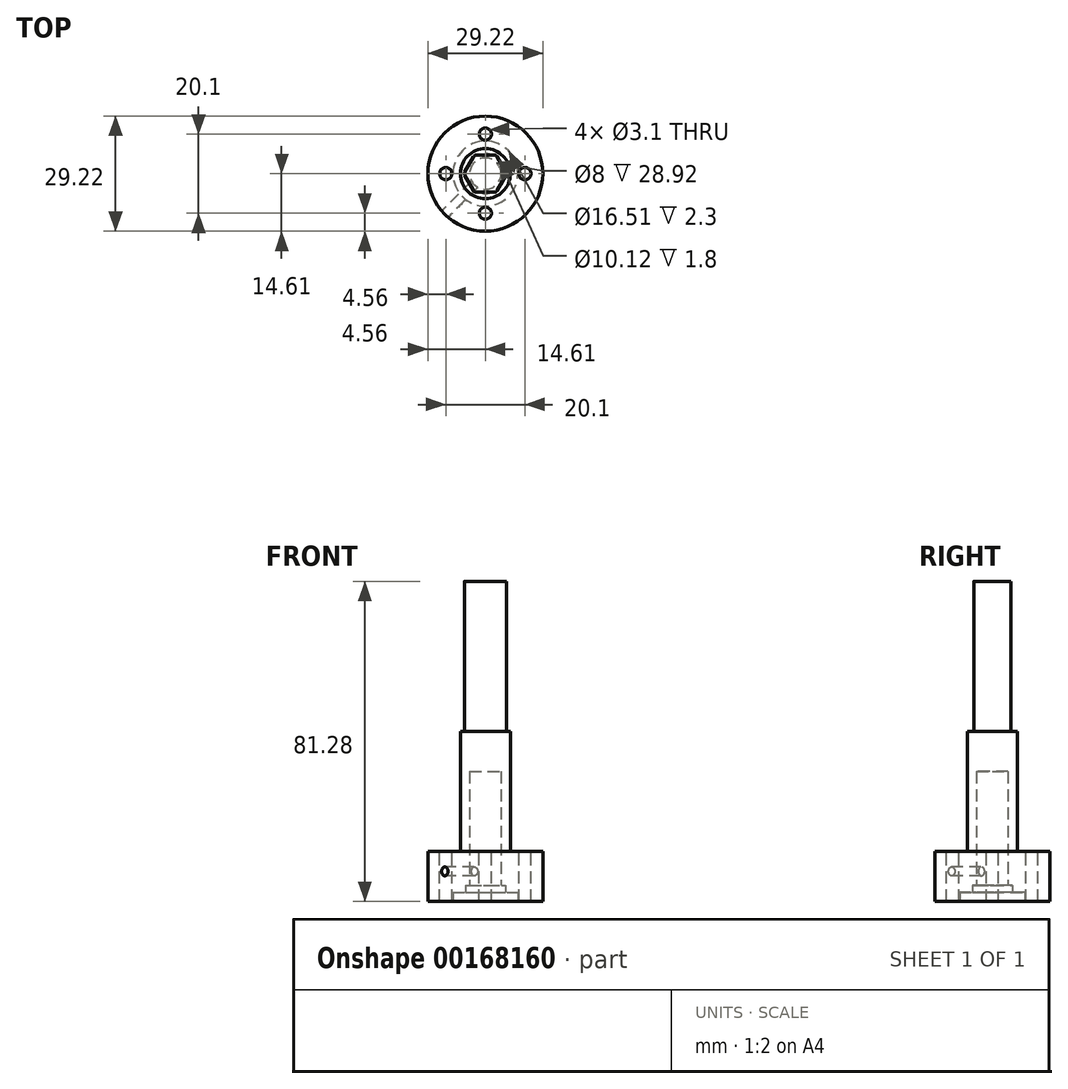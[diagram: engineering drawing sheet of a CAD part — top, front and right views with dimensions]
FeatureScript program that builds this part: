
annotation { "Feature Type Name" : "Feature", "Feature Type Description" : "" }
export const myFeature = defineFeature(function(context is Context, id is Id, definition is map)
    precondition{}
    {
        {
            var Q0;
            Q0=qCreatedBy(makeId("Top.planeOp"),FACE);
            var sketch = newSketch(context, id + "F0", { "sketchPlane" : qUnion([Q0])});
            skCircle(sketch, "E0", {"center": v(0, 0) * mm, "radius": 14.6 * mm});
            skSolve(sketch);
        }
        {
            var Q0;
            Q0=makeQuery(id+"F0.imprint","IMPRINT",FACE,{"disambiguationData":[TD([[makeQuery(id+"F0.imprint","IMPRINT",EDGE,{"derivedFrom":sQuery(id+"F0.wireOp",EDGE,"E0")}),1.0]])]});
            extrude(context, id + "F1", {"entities" : qUnion([Q0]), "depth" : 12.7 * mm});
        }
        {
            var Q0;
            Q0=makeQuery(id+"F1.opExtrude","CAP_FACE",FACE,{"disambiguationData":[OSD([sQuery(id+"F0.wireOp",EDGE,"E0")])],"isStart":false});
            var sketch = newSketch(context, id + "F2", { "sketchPlane" : qUnion([Q0])});
            skCircle(sketch, "E1", {"center": v(0, 0) * mm, "radius": 6.35 * mm});
            skSolve(sketch);
        }
        {
            var Q0;
            Q0=qSketchRegion(id+"F2",true);
            extrude(context, id + "F3", {"entities" : qUnion([Q0]), "operationType" : NewBodyOperationType.ADD, "depth" : 30.48 * mm});
        }
        {
            var Q0;
            Q0=makeQuery(id+"F3.opExtrude","CAP_FACE",FACE,{"disambiguationData":[OSD([sQuery(id+"F2.wireOp",EDGE,"E1")])],"isStart":false});
            var sketch = newSketch(context, id + "F4", { "sketchPlane" : qUnion([Q0])});
            skCircle(sketch, "E2.cCircle", {"center": v(0, 0) * mm, "radius": 4.72 * mm, "construction": true});
            skLineSegment(sketch, "E2.0", {"start": v(5.46, 0) * mm, "end": v(2.73, -4.72) * mm});
            skLineSegment(sketch, "E2.1", {"start": v(2.73, -4.72) * mm, "end": v(-2.73, -4.72) * mm});
            skLineSegment(sketch, "E2.2", {"start": v(-2.73, -4.72) * mm, "end": v(-5.46, 0) * mm});
            skLineSegment(sketch, "E2.3", {"start": v(-5.46, 0) * mm, "end": v(-2.73, 4.72) * mm});
            skLineSegment(sketch, "E2.4", {"start": v(-2.73, 4.72) * mm, "end": v(2.73, 4.72) * mm});
            skLineSegment(sketch, "E2.5", {"start": v(2.73, 4.72) * mm, "end": v(5.46, 0) * mm});
            skPoint(sketch, "E2.0.midPoint", {"position": v(4.1, -2.36) * mm});
            skSolve(sketch);
        }
        {
            var Q0;
            Q0=makeQuery(id+"F4.imprint","IMPRINT",FACE,{"disambiguationData":[TD([[makeQuery(id+"F4.imprint","IMPRINT",EDGE,{"derivedFrom":sQuery(id+"F4.wireOp",EDGE,"E2.0")}),-1.0]])]});
            extrude(context, id + "F5", {"entities" : qUnion([Q0]), "operationType" : NewBodyOperationType.ADD, "depth" : 38.1 * mm});
        }
        {
            var Q0;
            Q0=makeQuery(id+"F1.opExtrude","CAP_FACE",FACE,{"disambiguationData":[OSD([sQuery(id+"F0.wireOp",EDGE,"E0")])],"isStart":true});
            var sketch = newSketch(context, id + "F6", { "sketchPlane" : qUnion([Q0])});
            skCircle(sketch, "E3", {"center": v(0, 0) * mm, "radius": 8.26 * mm});
            skSolve(sketch);
        }
        {
            var Q0;
            Q0=qSketchRegion(id+"F6",true);
            extrude(context, id + "F7", {"entities" : qUnion([Q0]), "operationType" : NewBodyOperationType.REMOVE, "oppositeDirection" : true, "depth" : 2.3 * mm});
        }
        {
            var Q0;
            Q0=makeQuery(id+"F1.opExtrude","CAP_FACE",FACE,{"disambiguationData":[OSD([sQuery(id+"F0.wireOp",EDGE,"E0")])],"isStart":true});
            var sketch = newSketch(context, id + "F8", { "sketchPlane" : qUnion([Q0])});
            skCircle(sketch, "E4", {"center": v(0, 0) * mm, "radius": 5.06 * mm});
            skSolve(sketch);
        }
        {
            var Q0;
            Q0=qSketchRegion(id+"F8",true);
            extrude(context, id + "F9", {"entities" : qUnion([Q0]), "operationType" : NewBodyOperationType.REMOVE, "oppositeDirection" : true, "depth" : 4.1 * mm});
        }
        {
            var Q0;
            Q0=makeQuery(id+"F1.opExtrude","CAP_FACE",FACE,{"disambiguationData":[OSD([sQuery(id+"F0.wireOp",EDGE,"E0")])],"isStart":false});
            var sketch = newSketch(context, id + "F10", { "sketchPlane" : qUnion([Q0])});
            skPoint(sketch, "E5", {"position": v(-10.05, 0) * mm});
            skPoint(sketch, "E6", {"position": v(0, 10.05) * mm});
            skPoint(sketch, "E7", {"position": v(10.05, 0) * mm});
            skPoint(sketch, "E8", {"position": v(0, -10.05) * mm});
            skCircle(sketch, "E9", {"center": v(0, 0) * mm, "radius": 10.05 * mm, "construction": true});
            skSolve(sketch);
        }
        {
            var Q0;
            Q0=sQuery(id+"F10.wireOp",VERTEX,"E8");
            var Q1;
            Q1=sQuery(id+"F10.wireOp",VERTEX,"E5");
            var Q2;
            Q2=sQuery(id+"F10.wireOp",VERTEX,"E6");
            var Q3;
            Q3=sQuery(id+"F10.wireOp",VERTEX,"E7");
            var Q4;
            Q4=makeQuery(id+"F1.opExtrude","SWEPT_BODY",BODY,{"disambiguationData":[OSD([sQuery(id+"F0.wireOp",EDGE,"E0")])]});
            hole(context, id + "F11", {"style" : HoleStyle.SIMPLE, "endStyle" : HoleEndStyle.THROUGH, "holeDiameter" : 3.1 * mm, "locations" : qUnion([Q0, Q1, Q2, Q3]), "scope" : qUnion([Q4]), "isTappedThrough" : true});
        }
        {
            var Q0;
            Q0=makeQuery(id+"F5.opExtrude","SWEPT_EDGE",EDGE,{"disambiguationData":[OSD([sQuery(id+"F4.wireOp",EDGE,"E2.1"),sQuery(id+"F4.wireOp",EDGE,"E2.2")])]});
            var Q1;
            Q1=makeQuery(id+"F5.opExtrude","SWEPT_EDGE",EDGE,{"disambiguationData":[OSD([sQuery(id+"F4.wireOp",EDGE,"E2.0"),sQuery(id+"F4.wireOp",EDGE,"E2.1")])]});
            var Q2;
            Q2=makeQuery(id+"F5.opExtrude","SWEPT_EDGE",EDGE,{"disambiguationData":[OSD([sQuery(id+"F4.wireOp",EDGE,"E2.0"),sQuery(id+"F4.wireOp",EDGE,"E2.5")])]});
            var Q3;
            Q3=makeQuery(id+"F5.opExtrude","SWEPT_EDGE",EDGE,{"disambiguationData":[OSD([sQuery(id+"F4.wireOp",EDGE,"E2.4"),sQuery(id+"F4.wireOp",EDGE,"E2.5")])]});
            var Q4;
            Q4=makeQuery(id+"F5.opExtrude","SWEPT_EDGE",EDGE,{"disambiguationData":[OSD([sQuery(id+"F4.wireOp",EDGE,"E2.3"),sQuery(id+"F4.wireOp",EDGE,"E2.4")])]});
            var Q5;
            Q5=makeQuery(id+"F5.opExtrude","SWEPT_EDGE",EDGE,{"disambiguationData":[OSD([sQuery(id+"F4.wireOp",EDGE,"E2.2"),sQuery(id+"F4.wireOp",EDGE,"E2.3")])]});
            fillet(context, id + "F12", {"entities" : qUnion([Q0, Q1, Q2, Q3, Q4, Q5]), "radius" : 0.76 * mm, "tangentPropagation" : true, "allowEdgeOverflow" : false});
        }
        {
            var Q0;
            Q0=makeQuery(id+"F1.opExtrude","CAP_FACE",FACE,{"disambiguationData":[OSD([sQuery(id+"F0.wireOp",EDGE,"E0")])],"isStart":true});
            var sketch = newSketch(context, id + "F13", { "sketchPlane" : qUnion([Q0])});
            skCircle(sketch, "E10", {"center": v(0, 0) * mm, "radius": 4 * mm});
            skSolve(sketch);
        }
        {
            var Q0;
            Q0=qSketchRegion(id+"F13",true);
            extrude(context, id + "F14", {"entities" : qUnion([Q0]), "operationType" : NewBodyOperationType.REMOVE, "oppositeDirection" : true, "depth" : 33.02 * mm});
        }
        {
            var Q0;
            Q0=qCreatedBy(makeId("Front.planeOp"),FACE);
            var sketch = newSketch(context, id + "F15", { "sketchPlane" : qUnion([Q0])});
            skLineSegment(sketch, "E11", {"start": v(0, 0) * mm, "end": v(0, 37.16) * mm, "construction": true});
            skSolve(sketch);
        }
        {
            var Q0;
            Q0=sQuery(id+"F15.wireOp",EDGE,"E11");
            cPlane(context, id + "F16", {"entities" : qUnion([Q0]), "cplaneType" : CPlaneType.LINE_ANGLE, "offset" : 25.4 * mm, "angle" : 45 * degree, "width" : 152.4 * mm, "height" : 152.4 * mm});
        }
        {
            var Q0;
            Q0=makeQuery(id+"F1.opExtrude","CAP_FACE",FACE,{"disambiguationData":[OSD([sQuery(id+"F0.wireOp",EDGE,"E0")])],"isStart":false});
            var sketch = newSketch(context, id + "F17", { "sketchPlane" : qUnion([Q0])});
            skCircle(sketch, "E12.0", {"center": v(0, 0) * mm, "radius": 14.6 * mm, "construction": true});
            skLineSegment(sketch, "E13", {"start": v(0, 0) * mm, "end": v(-10.33, -10.33) * mm, "construction": true});
            skSolve(sketch);
        }
        {
            var Q0;
            Q0=qCreatedBy(id+"F16.planeOp",FACE);
            var Q1;
            Q1=sQuery(id+"F17.wireOp",VERTEX,"E13.end");
            cPlane(context, id + "F18", {"entities" : qUnion([Q0, Q1]), "cplaneType" : CPlaneType.PLANE_POINT, "offset" : 25.4 * mm, "width" : 152.4 * mm, "height" : 152.4 * mm});
        }
        {
            var Q0;
            Q0=qCreatedBy(id+"F18.planeOp",FACE);
            var sketch = newSketch(context, id + "F19", { "sketchPlane" : qUnion([Q0])});
            skLineSegment(sketch, "E14", {"start": v(0, 12.7) * mm, "end": v(0, 7.62) * mm, "construction": true});
            skPoint(sketch, "E15", {"position": v(0, 7.62) * mm});
            skSolve(sketch);
        }
        {
            var Q0;
            Q0=sQuery(id+"F19.wireOp",VERTEX,"E15");
            var Q1;
            Q1=makeQuery(id+"F1.opExtrude","SWEPT_BODY",BODY,{"disambiguationData":[OSD([sQuery(id+"F0.wireOp",EDGE,"E0")])]});
            hole(context, id + "F20", {"style" : HoleStyle.SIMPLE, "endStyle" : HoleEndStyle.BLIND, "oppositeDirection" : true, "standardTappedOrClearance" : lookupTablePath({ "standard" : "ANSI", "engagement" : "75%", "pitch" : "40 tpi", "size" : "#4", "type" : "Tapped" }), "standardBlindInLast" : lookupTablePath({ "standard" : "ANSI", "engagement" : "75%", "pitch" : "40 tpi", "size" : "#4", "type" : "Tapped" }), "holeDiameter" : 2.26 * mm, "holeDepth" : 12.7 * mm, "locations" : qUnion([Q0]), "scope" : qUnion([Q1]), "majorDiameter" : 2.84 * mm});
        }
    });
